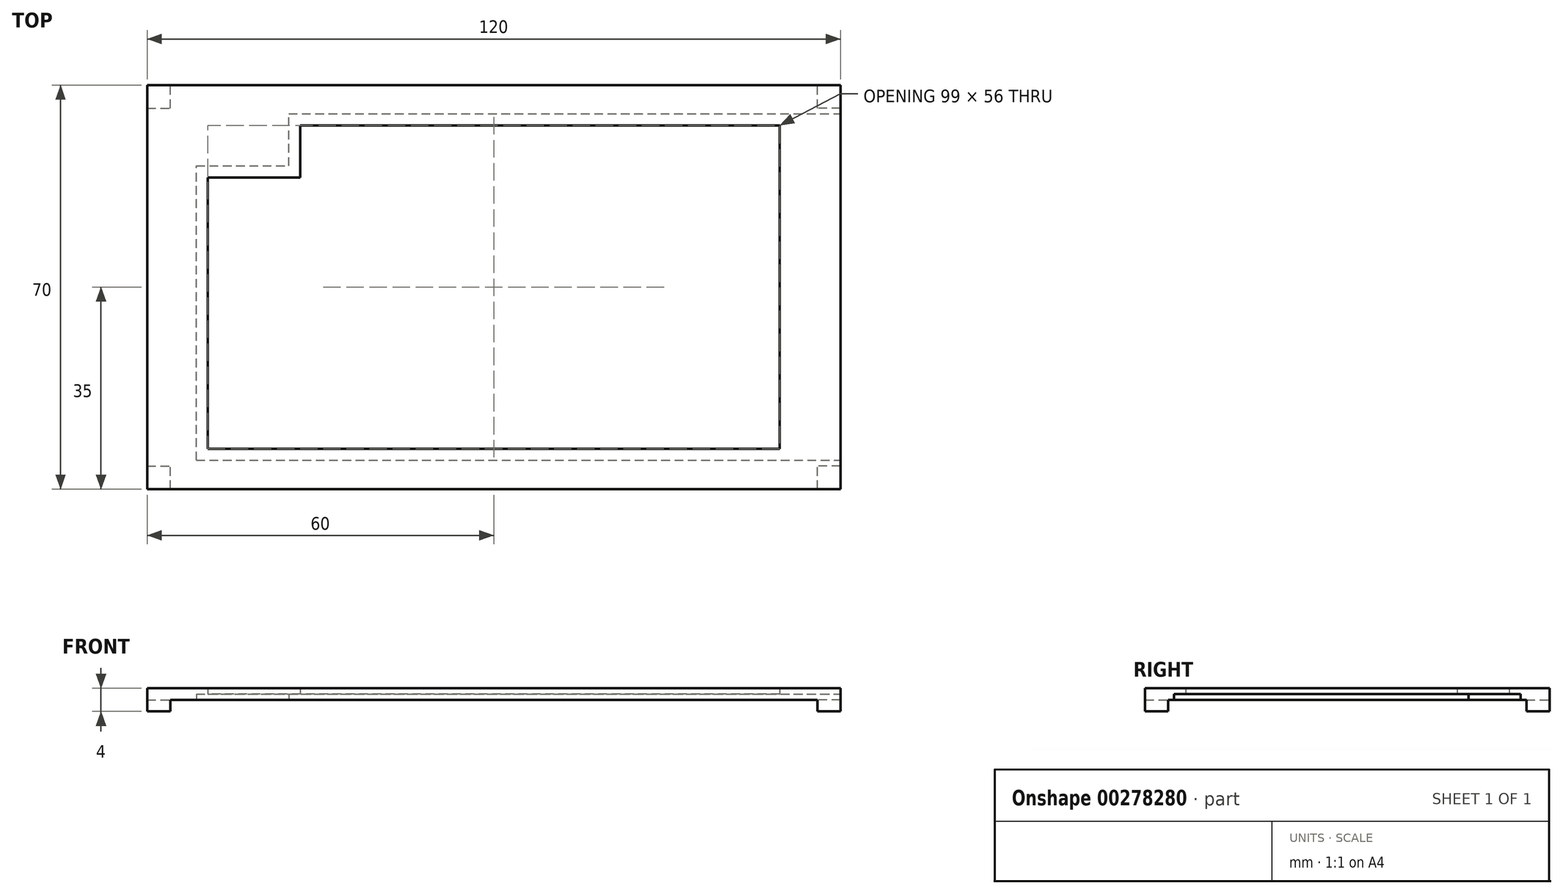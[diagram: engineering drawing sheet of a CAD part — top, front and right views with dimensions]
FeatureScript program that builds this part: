
annotation { "Feature Type Name" : "Feature", "Feature Type Description" : "" }
export const myFeature = defineFeature(function(context is Context, id is Id, definition is map)
    precondition{}
    {
        {
            var Q0;
            Q0=qCreatedBy(makeId("Top.planeOp"),FACE);
            var sketch = newSketch(context, id + "F0", { "sketchPlane" : qUnion([Q0])});
            skLineSegment(sketch, "E0.bottom", {"start": v(0, 0) * mm, "end": v(87, 0) * mm, "construction": true});
            skLineSegment(sketch, "E0.top", {"start": v(0, 60) * mm, "end": v(87, 60) * mm, "construction": true});
            skLineSegment(sketch, "E0.left", {"start": v(0, 0) * mm, "end": v(0, 60) * mm, "construction": true});
            skLineSegment(sketch, "E0.right", {"start": v(87, 0) * mm, "end": v(87, 60) * mm, "construction": true});
            skLineSegment(sketch, "E1.bottom", {"start": v(-16, 51) * mm, "end": v(25, 51) * mm, "construction": true});
            skLineSegment(sketch, "E1.top", {"start": v(-16, 0) * mm, "end": v(25, 0) * mm, "construction": true});
            skLineSegment(sketch, "E1.left", {"start": v(-16, 51) * mm, "end": v(-16, 0) * mm, "construction": true});
            skLineSegment(sketch, "E1.right", {"start": v(25, 51) * mm, "end": v(25, 0) * mm, "construction": true});
            skLineSegment(sketch, "E2.bottom", {"start": v(-24.5, 65) * mm, "end": v(95.5, 65) * mm});
            skLineSegment(sketch, "E2.top", {"start": v(-24.5, -5) * mm, "end": v(95.5, -5) * mm});
            skLineSegment(sketch, "E2.left", {"start": v(-24.5, 65) * mm, "end": v(-24.5, -5) * mm});
            skLineSegment(sketch, "E2.right", {"start": v(95.5, 65) * mm, "end": v(95.5, -5) * mm});
            skLineSegment(sketch, "E3", {"start": v(-16, 0) * mm, "end": v(-24.5, 0) * mm, "construction": true});
            skLineSegment(sketch, "E4", {"start": v(87, 0) * mm, "end": v(95.5, 0) * mm, "construction": true});
            skLineSegment(sketch, "E5", {"start": v(87, 60) * mm, "end": v(87, 65) * mm, "construction": true});
            skLineSegment(sketch, "E6", {"start": v(87, 0) * mm, "end": v(87, -5) * mm, "construction": true});
            skLineSegment(sketch, "E7", {"start": v(2, 58) * mm, "end": v(85, 58) * mm});
            skLineSegment(sketch, "E8", {"start": v(85, 58) * mm, "end": v(85, 2) * mm});
            skLineSegment(sketch, "E9", {"start": v(85, 2) * mm, "end": v(-14, 2) * mm});
            skLineSegment(sketch, "E10", {"start": v(-14, 2) * mm, "end": v(-14, 49) * mm});
            skLineSegment(sketch, "E11", {"start": v(-14, 49) * mm, "end": v(2, 49) * mm});
            skLineSegment(sketch, "E12", {"start": v(2, 49) * mm, "end": v(2, 58) * mm});
            skSolve(sketch);
        }
        {
            var Q0;
            Q0 = qSketchRegion(id + "F0", true);
            extrude(context, id + "F1", {"entities" : qUnion([Q0]), "depth" : 2 * mm});
        }
        {
            var Q0;
            Q0=makeQuery(id+"F1.opExtrude","CAP_FACE",FACE,{"disambiguationData":[OSD([sQuery(id+"F0.wireOp",EDGE,"E2.bottom"),sQuery(id+"F0.wireOp",EDGE,"E2.top"),sQuery(id+"F0.wireOp",EDGE,"E2.left"),sQuery(id+"F0.wireOp",EDGE,"E2.right"),sQuery(id+"F0.wireOp",EDGE,"E7"),sQuery(id+"F0.wireOp",EDGE,"E8"),sQuery(id+"F0.wireOp",EDGE,"E9"),sQuery(id+"F0.wireOp",EDGE,"E10"),sQuery(id+"F0.wireOp",EDGE,"E11"),sQuery(id+"F0.wireOp",EDGE,"E12")])],"isStart":true});
            var sketch = newSketch(context, id + "F2", { "sketchPlane" : qUnion([Q0])});
            skLineSegment(sketch, "E13.bottom", {"start": v(-16, 0) * mm, "end": v(95.5, 0) * mm});
            skLineSegment(sketch, "E13.top", {"start": v(0, -60) * mm, "end": v(95.5, -60) * mm});
            skLineSegment(sketch, "E13.left", {"start": v(-16, 0) * mm, "end": v(-16, -51) * mm});
            skLineSegment(sketch, "E13.right", {"start": v(95.5, 0) * mm, "end": v(95.5, -60) * mm});
            skLineSegment(sketch, "E14", {"start": v(-16, -51) * mm, "end": v(0, -51) * mm});
            skLineSegment(sketch, "E15", {"start": v(0, -51) * mm, "end": v(0, -60) * mm});
            skSolve(sketch);
        }
        {
            var Q0;
            Q0 = qSketchRegion(id + "F2", true);
            extrude(context, id + "F3", {"entities" : qUnion([Q0]), "operationType" : NewBodyOperationType.REMOVE, "oppositeDirection" : true, "depth" : 1 * mm});
        }
        {
            var Q0;
            Q0=makeQuery(id+"F1.opExtrude","CAP_FACE",FACE,{"disambiguationData":[OSD([sQuery(id+"F0.wireOp",EDGE,"E2.bottom"),sQuery(id+"F0.wireOp",EDGE,"E2.top"),sQuery(id+"F0.wireOp",EDGE,"E2.left"),sQuery(id+"F0.wireOp",EDGE,"E2.right"),sQuery(id+"F0.wireOp",EDGE,"E7"),sQuery(id+"F0.wireOp",EDGE,"E8"),sQuery(id+"F0.wireOp",EDGE,"E9"),sQuery(id+"F0.wireOp",EDGE,"E10"),sQuery(id+"F0.wireOp",EDGE,"E11"),sQuery(id+"F0.wireOp",EDGE,"E12")])],"isStart":true});
            var sketch = newSketch(context, id + "F4", { "sketchPlane" : qUnion([Q0])});
            skLineSegment(sketch, "E16.bottom", {"start": v(-24.5, 5) * mm, "end": v(-20.5, 5) * mm});
            skLineSegment(sketch, "E16.top", {"start": v(-24.5, 1) * mm, "end": v(-20.5, 1) * mm});
            skLineSegment(sketch, "E16.left", {"start": v(-24.5, 5) * mm, "end": v(-24.5, 1) * mm});
            skLineSegment(sketch, "E16.right", {"start": v(-20.5, 5) * mm, "end": v(-20.5, 1) * mm});
            skLineSegment(sketch, "E17", {"start": v(35.5, 5) * mm, "end": v(35.5, -65) * mm, "construction": true});
            skLineSegment(sketch, "E18.MirrorCS", {"start": v(-24.5, -61) * mm, "end": v(-24.5, -65) * mm});
            skLineSegment(sketch, "E19.MirrorCS", {"start": v(-20.5, -61) * mm, "end": v(-20.5, -65) * mm});
            skLineSegment(sketch, "E20.MirrorCS", {"start": v(-24.5, -65) * mm, "end": v(-20.5, -65) * mm});
            skLineSegment(sketch, "E21.MirrorCS", {"start": v(-24.5, -61) * mm, "end": v(-20.5, -61) * mm});
            skLineSegment(sketch, "E22.MirrorCS", {"start": v(95.5, 5) * mm, "end": v(91.5, 5) * mm});
            skLineSegment(sketch, "E23.MirrorCS", {"start": v(95.5, -61) * mm, "end": v(91.5, -61) * mm});
            skLineSegment(sketch, "E24.MirrorCS", {"start": v(95.5, 1) * mm, "end": v(91.5, 1) * mm});
            skLineSegment(sketch, "E25.MirrorCS", {"start": v(95.5, -65) * mm, "end": v(91.5, -65) * mm});
            skLineSegment(sketch, "E26.MirrorCS", {"start": v(95.5, 5) * mm, "end": v(95.5, 1) * mm});
            skLineSegment(sketch, "E27.MirrorCS", {"start": v(91.5, 5) * mm, "end": v(91.5, 1) * mm});
            skLineSegment(sketch, "E28.MirrorCS", {"start": v(95.5, -61) * mm, "end": v(95.5, -65) * mm});
            skLineSegment(sketch, "E29.MirrorCS", {"start": v(91.5, -61) * mm, "end": v(91.5, -65) * mm});
            skSolve(sketch);
        }
        {
            var Q0;
            Q0 = qSketchRegion(id + "F4", true);
            extrude(context, id + "F5", {"entities" : qUnion([Q0]), "operationType" : NewBodyOperationType.ADD, "depth" : 2 * mm});
        }
    });
